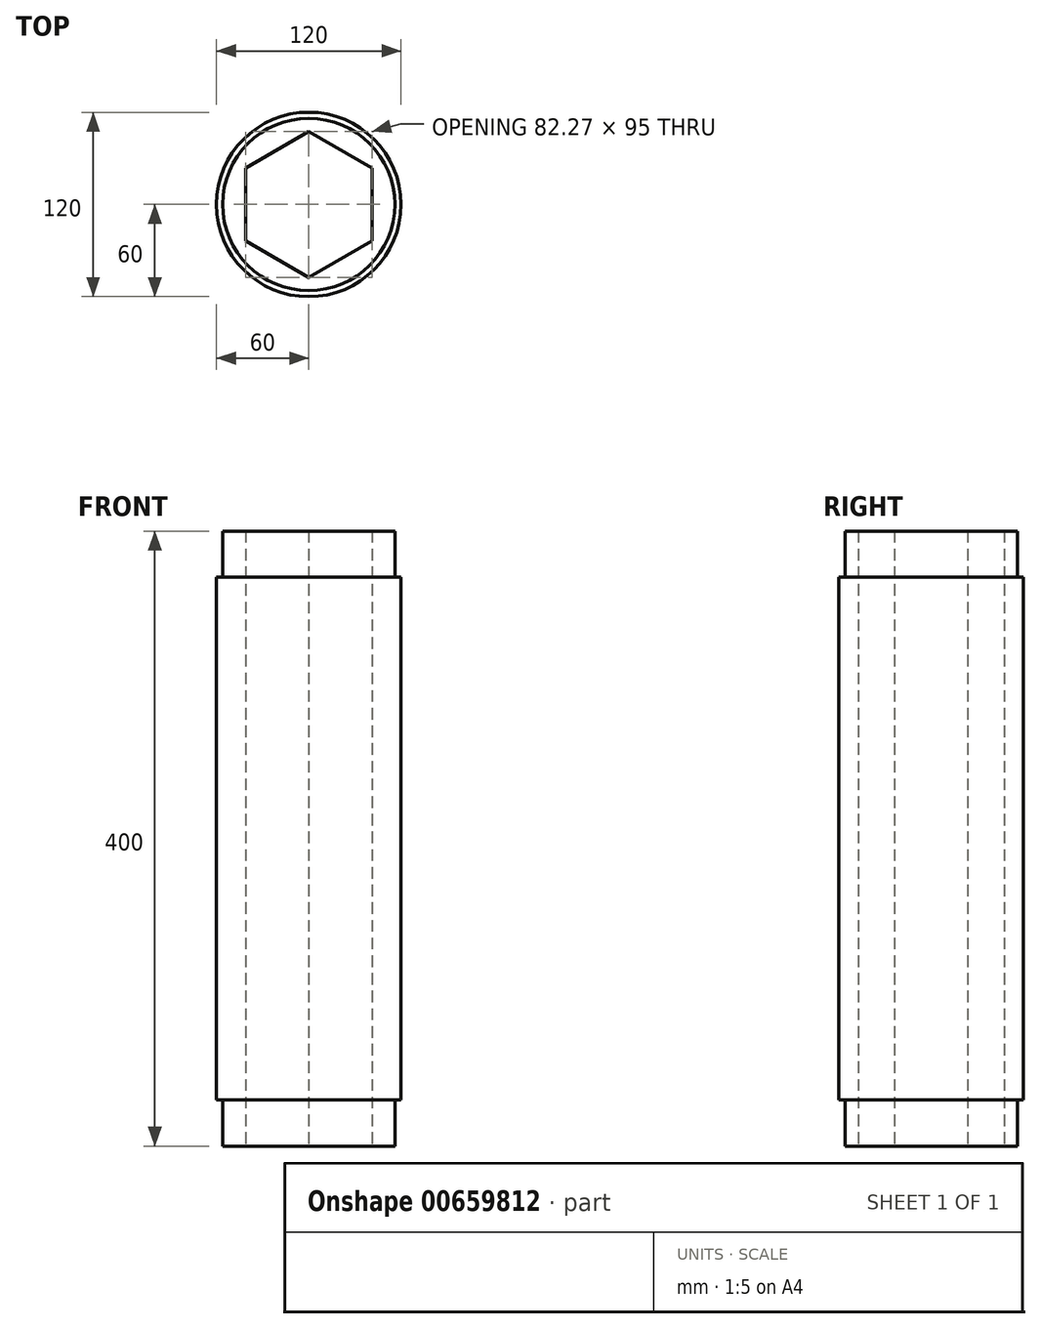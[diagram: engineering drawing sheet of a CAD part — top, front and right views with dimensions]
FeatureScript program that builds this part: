
annotation { "Feature Type Name" : "Feature", "Feature Type Description" : "" }
export const myFeature = defineFeature(function(context is Context, id is Id, definition is map)
    precondition{}
    {
        {
            var Q0;
            Q0=qCreatedBy(makeId("Top.planeOp"),FACE);
            var sketch = newSketch(context, id + "F0", { "sketchPlane" : qUnion([Q0])});
            skCircle(sketch, "E0", {"center": v(0, 0) * mm, "radius": 62.5 * mm, "construction": true});
            skCircle(sketch, "E1", {"center": v(0, 0) * mm, "radius": 47.5 * mm, "construction": true});
            skLineSegment(sketch, "E2.0", {"start": v(62.5, 36.08) * mm, "end": v(62.5, -36.08) * mm});
            skLineSegment(sketch, "E2.1", {"start": v(62.5, -36.08) * mm, "end": v(0, -72.17) * mm});
            skLineSegment(sketch, "E2.2", {"start": v(0, -72.17) * mm, "end": v(-62.5, -36.08) * mm});
            skLineSegment(sketch, "E2.3", {"start": v(-62.5, -36.08) * mm, "end": v(-62.5, 36.08) * mm});
            skLineSegment(sketch, "E2.4", {"start": v(-62.5, 36.08) * mm, "end": v(0, 72.17) * mm});
            skLineSegment(sketch, "E2.5", {"start": v(0, 72.17) * mm, "end": v(62.5, 36.08) * mm});
            skPoint(sketch, "E2.0.midPoint", {"position": v(62.5, 0) * mm});
            skLineSegment(sketch, "E3", {"start": v(0, 0) * mm, "end": v(62.5, -36.08) * mm, "construction": true});
            skLineSegment(sketch, "E4", {"start": v(0, 0) * mm, "end": v(62.5, 36.08) * mm, "construction": true});
            skLineSegment(sketch, "E5", {"start": v(41.14, -23.75) * mm, "end": v(41.14, 23.75) * mm});
            skLineSegment(sketch, "E6", {"start": v(41.14, 23.75) * mm, "end": v(0, 47.5) * mm});
            skLineSegment(sketch, "E7", {"start": v(0, 0) * mm, "end": v(-62.5, 36.08) * mm, "construction": true});
            skLineSegment(sketch, "E8", {"start": v(0, 0) * mm, "end": v(-62.5, -36.08) * mm, "construction": true});
            skLineSegment(sketch, "E9", {"start": v(0, 0) * mm, "end": v(0, -72.17) * mm, "construction": true});
            skLineSegment(sketch, "E10", {"start": v(0, 0) * mm, "end": v(0, 72.17) * mm, "construction": true});
            skLineSegment(sketch, "E11", {"start": v(0, 47.5) * mm, "end": v(-41.14, 23.75) * mm});
            skLineSegment(sketch, "E12", {"start": v(-41.14, 23.75) * mm, "end": v(-41.14, -23.75) * mm});
            skLineSegment(sketch, "E13", {"start": v(-41.14, -23.75) * mm, "end": v(0, -47.5) * mm});
            skLineSegment(sketch, "E14", {"start": v(0, -47.5) * mm, "end": v(41.14, -23.75) * mm});
            skSolve(sketch);
        }
        {
            var Q0;
            Q0 = qSketchRegion(id + "F0", true);
            extrude(context, id + "F1", {"entities" : qUnion([Q0]), "depth" : 400 * mm, "offsetDistance" : 25 * mm});
        }
        {
            var Q0;
            Q0=qCreatedBy(makeId("Top.planeOp"),FACE);
            var sketch = newSketch(context, id + "F2", { "sketchPlane" : qUnion([Q0])});
            skCircle(sketch, "E15", {"center": v(0, 0) * mm, "radius": 60 * mm});
            skCircle(sketch, "E16", {"center": v(0, 0) * mm, "radius": 91.56 * mm});
            skSolve(sketch);
        }
        {
            var Q0;
            Q0 = qSketchRegion(id + "F2", true);
            extrude(context, id + "F3", {"entities" : qUnion([Q0]), "operationType" : NewBodyOperationType.REMOVE, "endBound" : BoundingType.THROUGH_ALL, "depth" : 25 * mm, "offsetDistance" : 25 * mm});
        }
        {
            var Q0;
            Q0=qCreatedBy(makeId("Top.planeOp"),FACE);
            var sketch = newSketch(context, id + "F4", { "sketchPlane" : qUnion([Q0])});
            skCircle(sketch, "E17", {"center": v(0, 0) * mm, "radius": 159.33 * mm});
            skCircle(sketch, "E18", {"center": v(0, 0) * mm, "radius": 56 * mm});
            skSolve(sketch);
        }
        {
            var Q0;
            Q0 = qSketchRegion(id + "F4", true);
            extrude(context, id + "F5", {"entities" : qUnion([Q0]), "operationType" : NewBodyOperationType.REMOVE, "depth" : 30 * mm, "offsetDistance" : 25 * mm});
        }
        {
            var Q0;
            Q0=makeQuery(id+"F1.opExtrude","CAP_FACE",FACE,{"disambiguationData":[OSD([sQuery(id+"F0.wireOp",EDGE,"E2.0"),sQuery(id+"F0.wireOp",EDGE,"E2.1"),sQuery(id+"F0.wireOp",EDGE,"E2.2"),sQuery(id+"F0.wireOp",EDGE,"E2.3"),sQuery(id+"F0.wireOp",EDGE,"E2.4"),sQuery(id+"F0.wireOp",EDGE,"E2.5"),sQuery(id+"F0.wireOp",EDGE,"E5"),sQuery(id+"F0.wireOp",EDGE,"E6"),sQuery(id+"F0.wireOp",EDGE,"E11"),sQuery(id+"F0.wireOp",EDGE,"E12"),sQuery(id+"F0.wireOp",EDGE,"E13"),sQuery(id+"F0.wireOp",EDGE,"E14")])],"isStart":false});
            var sketch = newSketch(context, id + "F6", { "sketchPlane" : qUnion([Q0])});
            skCircle(sketch, "E19.0", {"center": v(0, 0) * mm, "radius": 60 * mm, "construction": true});
            skCircle(sketch, "E20", {"center": v(0, 0) * mm, "radius": 56 * mm});
            skCircle(sketch, "E21", {"center": v(0, 0) * mm, "radius": 72.94 * mm});
            skSolve(sketch);
        }
        {
            var Q0;
            Q0 = qSketchRegion(id + "F6", true);
            extrude(context, id + "F7", {"entities" : qUnion([Q0]), "operationType" : NewBodyOperationType.REMOVE, "oppositeDirection" : true, "depth" : 30 * mm, "offsetDistance" : 25 * mm});
        }
    });
